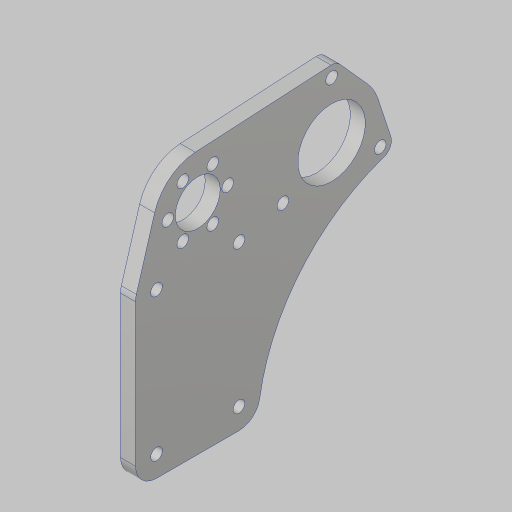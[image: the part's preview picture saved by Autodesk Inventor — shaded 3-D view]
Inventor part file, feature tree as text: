
AUTODESK INVENTOR PART (.ipt)
format: ipt  version: 2023.5 (Build 275446000, 446)  size: 176,128 bytes
history: native  units: in
note: dims shown in document units (in); Inventor stores cm internally (conversion verified against a paired STEP export)
features: sketch x2, hole x2, extrude x1
ambient origin geometry x8: Origin, YZ Plane, XZ Plane, XY Plane, X Axis, Y Axis, Z Axis, Center Point
bodies: Solid1 (feature_tree)
feature tree (5):
  sketch  "Sketch1"  dims[d0=3.0in d1=2.2in]
  sketch  "Sketch2"  dims[d2=3.0in d3=2.375in d4=1.375in d5=0.201in d6=0.201in d7=0.201in d8=0.201in d9=1.0in d10=1.0in d11=3.0in d12=2.3622in d14=360.0deg d16=1.125in d17=2.246in d18=0.75in d19=2.402in d20=0.75in d21=0.25in d22=0.25in d23=0.25in d24=0.25in d25=0.0in d33=0.196in d34=0.75in d35=0.375in d36=0.25in d37=0.5635in d38=1.0in d39=0.8108in d40=0.375in d41=1.1811in d43=360.0deg d45=0.375in d46=0.375in d47=0.375in d48=3.1in d49=0.196in d50=0.75in d51=0.385in d52=0.25in d53=0.5635in d54=1.0in d55=0.8108in]
  extrude  "Extrusion1"  Depth=2.2in
  hole  "Motor Mount Holes"  [1 undecoded]
  hole  "Hole3"  [1 undecoded]
note: 2 required parameter values undecoded (feature->parameter linkage not recoverable at this tier; creation-order binding heuristic only, values carry confidence <= 0.55)
